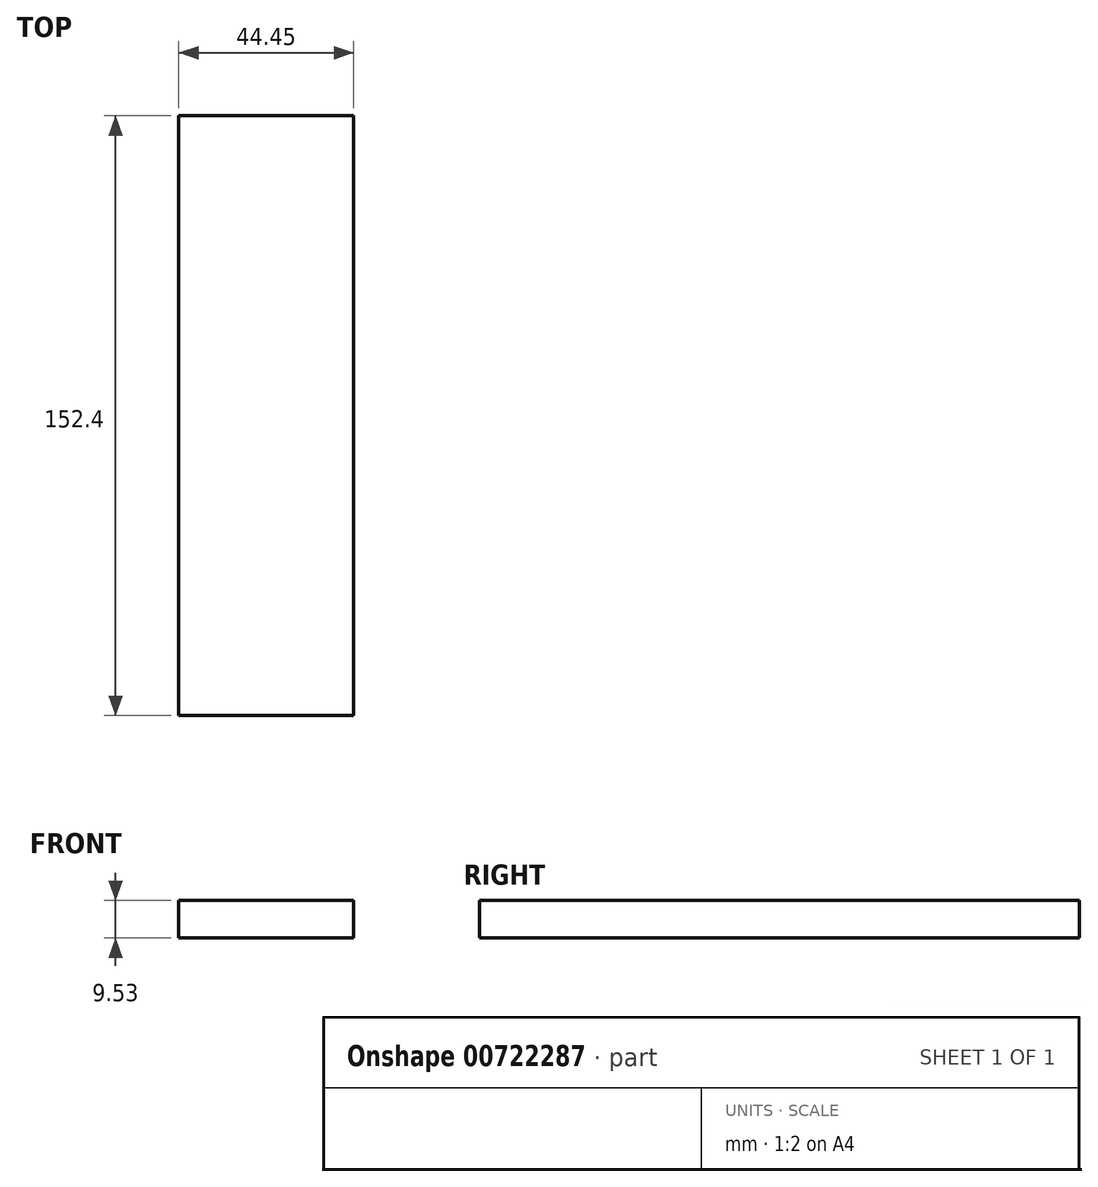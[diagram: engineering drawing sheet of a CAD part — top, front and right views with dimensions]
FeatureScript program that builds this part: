
annotation { "Feature Type Name" : "Feature", "Feature Type Description" : "" }
export const myFeature = defineFeature(function(context is Context, id is Id, definition is map)
    precondition{}
    {
        {
            var Q0;
            Q0=qCreatedBy(makeId("Top.planeOp"),FACE);
            var sketch = newSketch(context, id + "F0", { "sketchPlane" : qUnion([Q0])});
            skLineSegment(sketch, "E0.bottom", {"start": v(0, 0) * mm, "end": v(44.45, 0) * mm});
            skLineSegment(sketch, "E0.top", {"start": v(0, -152.4) * mm, "end": v(44.45, -152.4) * mm});
            skLineSegment(sketch, "E0.left", {"start": v(0, 0) * mm, "end": v(0, -152.4) * mm});
            skLineSegment(sketch, "E0.right", {"start": v(44.45, 0) * mm, "end": v(44.45, -152.4) * mm});
            skSolve(sketch);
        }
        {
            var Q0;
            Q0=makeQuery(id+"F0.imprint","IMPRINT",FACE,{"disambiguationData":[TD([[makeQuery(id+"F0.imprint","IMPRINT",EDGE,{"derivedFrom":sQuery(id+"F0.wireOp",EDGE,"E0.bottom")}),-1.0]])]});
            extrude(context, id + "F1", {"entities" : qUnion([Q0]), "depth" : 9.52 * mm, "offsetDistance" : 25.4 * mm});
        }
    });
